# Revit family: NBS_DudleyIndustriesLimited_HndDriers_SlimLineRecessedWarmAirDryer
name_source: partatom
category: Specialty Equipment
revit_build: Autodesk Revit 2016 (Build: 20150220_1215(x64)
units: mm (PartAtom-declared; Revit-internal decimal feet)

## family parameters
Cut with Voids When Loaded = Yes
Host = Face
Part Type = Normal
Room Calculation Point = No
Round Connector Dimension = Use Diameter
Shared = No

## types (1)
- Slim Line Recessed Warm Air Dryer
    AirOutput = 21 m/s
    AssetType = Fixed
    BIMObjectName = NBS_DudleyIndustriesLimited_HandDriers_SlimLineRecessedWarmAirDryer
    BodyColourAndFinish = Satin stainless steel
    BodyEnclosure = 304 Stainless steel
    BodyIngressProtectionMinimum = IP21
    Category = Pr_40_70_62_37:Hand driers
    CodePerformance = CE Marked, BS EN 60335-2-23:2003 + *A1:2008 (Particular Requirements for Appliances for skin and hair Care) and BSEN60335-1:2002 + *A2:2006 (incorporating *A1,*A11,*A12, *A13 (Safety of Household and similar electrical appliances), EN55014-1: 2006 + A1: 2009*, EN55014-2: 1997 + A1: 2001 + A2:2008*, EN61000-3-2: 2006, EN61000-3-3: 2008*, Tests marked * are not covered under SGS UKAS Scope, RoHS, WEEE
    Color = Satin stainless steel
    Default Elevation = 1000 mm  [stored 3.28084 ft]
    Description = Stylish satin stainless steel warm air dryer
    DurationUnit = year
    ElectricalDeviceNominalPower = 0
    EquipmentElectricalPower = 208–240 V AC, 1400–1900 W
    ExpectedLife = 10
    Features = Clean ergonomic design, Suitable for 100mm wall cavities, Durable stainless steel enclosure, Seam welded fabrication, Integral painted metal liner, Available as an individual unit or with Waste Bin and Paper Towel dispenser, 'No' Touch Automatic operation by infrared sensor built into the air outlet, Automatic start/stop, CE Marked, RoHS, WEEE
    Form = Recessed, Wall mounted
    HandDryerMaterial = NBS_Concept
    HandDryingTime = 15-20 s
    HasProtectiveEarth = Yes
    IfcExportAs = IfcElectricApplianceType
    IfcExportType = HANDDRYER
    MainColor = Satin stainless steel
    ManufacturerName = Dudley Industries Limited
    ManufacturerURL = www.dudleyindustries.com
    Material = Brushed stainless steel
    ModelNumber = 92282SS
    ModelReference = Slimline Recessed Warm Air Dryer
    NBSCertification = www.nationalbimlibrary.com/cert/1houb24l
    NBSDescription = Hand driers
    NBSReference = 45-35-72/334
    Name = HandDriers_SlimLineRecessedWarmAirDryer_DudleyIndustriesLimited
    NoiseLevelAtOneMetre = 81.5 dBA
    NominalCurrent = 0
    NominalDepth = 116 mm  [stored 0.380577 ft]
    NominalHeight = 579 mm  [stored 1.89961 ft]
    NominalLength = 382 mm  [stored 1.25328 ft]
    NominalWidth = 382 mm  [stored 1.25328 ft]
    NumberOfPoles = 0
    Operation = Automatic. No touch
    PhaseAngle = 0.00°
    PowerRating = 1400–1900 W
    ProductInformation = www.dudleyindustries.com/product/slim-line-recessed-warm-air-dryer/
    Style = Hand Dryer
    SustainabilityPerformance = 100% Recycleable
    Uniclass2015Code = Pr_40_70_62_37
    Uniclass2015Title = Hand driers
    Uniclass2015Version = Products v1.4
    UsageCurrent = 0
    Version = 3
    WarrantyDescription = Parts & Labour
    WarrantyDurationLabor = year
    WarrantyDurationParts = year
    WarrantyDurationUnit = year
    WarrantyGuarantorLabor = 5
    WarrantyGuarantorParts = 5
    Weight = 14.3 kg

note: [stored X ft] marks values corroborated as IEEE doubles in the binary element streams (Revit-internal decimal feet)

## geometry (parser evidence)
native form markers: Sweep x2
no freeform markers — native parametric forms only
